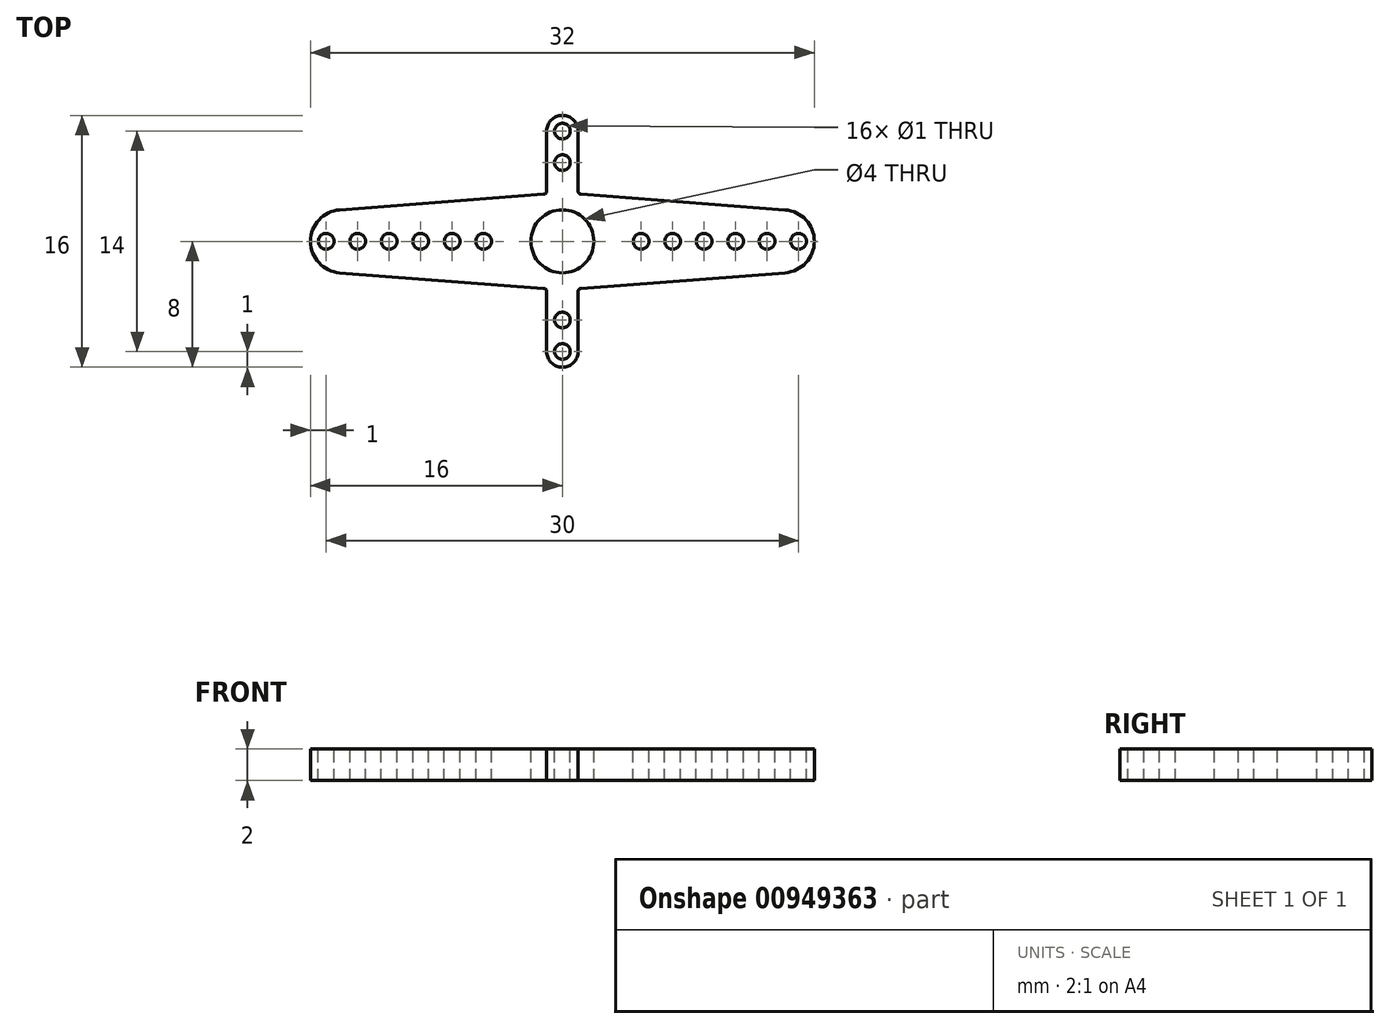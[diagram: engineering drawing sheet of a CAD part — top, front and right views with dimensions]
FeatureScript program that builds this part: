
annotation { "Feature Type Name" : "Feature", "Feature Type Description" : "" }
export const myFeature = defineFeature(function(context is Context, id is Id, definition is map)
    precondition{}
    {
        {
            var Q0;
            Q0=qCreatedBy(makeId("Top.planeOp"),FACE);
            var sketch = newSketch(context, id + "F0", { "sketchPlane" : qUnion([Q0])});
            skLineSegment(sketch, "E0", {"start": v(0, 0) * mm, "end": v(16, 0) * mm, "construction": true});
            skPoint(sketch, "E1", {"position": v(5, 0) * mm});
            skLineSegment(sketch, "E2", {"start": v(0, 0) * mm, "end": v(0, 8) * mm, "construction": true});
            skPoint(sketch, "E3", {"position": v(0, 5) * mm});
            skLineSegment(sketch, "E4", {"start": v(1, 7) * mm, "end": v(1, 3.19) * mm});
            skLineSegment(sketch, "E5", {"start": v(14.15, 2) * mm, "end": v(1.18, 2.99) * mm});
            skPoint(sketch, "E6.MirrorP", {"position": v(-5, 0) * mm});
            skLineSegment(sketch, "E7.MirrorCS", {"start": v(0, 0) * mm, "end": v(-16, 0) * mm, "construction": true});
            skLineSegment(sketch, "E8.MirrorCS", {"start": v(-14.15, 2) * mm, "end": v(-1.18, 2.99) * mm});
            skLineSegment(sketch, "E9.MirrorCS", {"start": v(-1, 7) * mm, "end": v(-1, 3.19) * mm});
            skPoint(sketch, "E10.visualSharp", {"position": v(1, 3) * mm});
            skArc(sketch, "E10.filletArc", {"start": v(1, 3.19) * mm, "mid": v(1.05, 3.05) * mm, "end": v(1.18, 2.99) * mm});
            skPoint(sketch, "E11.visualSharp", {"position": v(-1, 3) * mm});
            skArc(sketch, "E11.filletArc", {"start": v(-1.18, 2.99) * mm, "mid": v(-1.05, 3.05) * mm, "end": v(-1, 3.19) * mm});
            skArc(sketch, "E12", {"start": v(1, 7) * mm, "mid": v(0, 8) * mm, "end": v(-1, 7) * mm});
            skArc(sketch, "E13.MirrorCS", {"start": v(1, -3.19) * mm, "mid": v(1.05, -3.05) * mm, "end": v(1.18, -2.99) * mm});
            skArc(sketch, "E14.MirrorCS", {"start": v(-1.18, -2.99) * mm, "mid": v(-1.05, -3.05) * mm, "end": v(-1, -3.19) * mm});
            skPoint(sketch, "E15.MirrorP", {"position": v(0, -5) * mm});
            skLineSegment(sketch, "E16.MirrorCS", {"start": v(-1, -7) * mm, "end": v(-1, -3.19) * mm});
            skPoint(sketch, "E17.MirrorP", {"position": v(-1, -3) * mm});
            skLineSegment(sketch, "E18.MirrorCS", {"start": v(14.15, -2) * mm, "end": v(1.18, -2.99) * mm});
            skArc(sketch, "E19.MirrorCS", {"start": v(1, -7) * mm, "mid": v(0, -8) * mm, "end": v(-1, -7) * mm});
            skPoint(sketch, "E20.MirrorP", {"position": v(1, -3) * mm});
            skLineSegment(sketch, "E21.MirrorCS", {"start": v(1, -7) * mm, "end": v(1, -3.19) * mm});
            skLineSegment(sketch, "E22.MirrorCS", {"start": v(-14.15, -2) * mm, "end": v(-1.18, -2.99) * mm});
            skArc(sketch, "E23", {"start": v(14.15, -2) * mm, "mid": v(16, 0) * mm, "end": v(14.15, 2) * mm});
            skArc(sketch, "E24.MirrorCS", {"start": v(-14.15, -2) * mm, "mid": v(-16, 0) * mm, "end": v(-14.15, 2) * mm});
            skSolve(sketch);
        }
        {
            var Q0;
            Q0=makeQuery(id+"F0.imprint","IMPRINT",FACE,{"disambiguationData":[TD([[makeQuery(id+"F0.imprint","IMPRINT",EDGE,{"derivedFrom":sQuery(id+"F0.wireOp",EDGE,"E4")}),-1.0]])]});
            extrude(context, id + "F1", {"entities" : qUnion([Q0]), "depth" : 2 * mm, "offsetDistance" : 25 * mm});
        }
        {
            var Q0;
            Q0=makeQuery(id+"F1.opExtrude","CAP_FACE",FACE,{"disambiguationData":[OSD([sQuery(id+"F0.wireOp",EDGE,"E4"),sQuery(id+"F0.wireOp",EDGE,"E5"),sQuery(id+"F0.wireOp",EDGE,"E8.MirrorCS"),sQuery(id+"F0.wireOp",EDGE,"E9.MirrorCS"),sQuery(id+"F0.wireOp",EDGE,"E10.filletArc"),sQuery(id+"F0.wireOp",EDGE,"E11.filletArc"),sQuery(id+"F0.wireOp",EDGE,"E12"),sQuery(id+"F0.wireOp",EDGE,"E13.MirrorCS"),sQuery(id+"F0.wireOp",EDGE,"E14.MirrorCS"),sQuery(id+"F0.wireOp",EDGE,"E16.MirrorCS"),sQuery(id+"F0.wireOp",EDGE,"E18.MirrorCS"),sQuery(id+"F0.wireOp",EDGE,"E19.MirrorCS"),sQuery(id+"F0.wireOp",EDGE,"E21.MirrorCS"),sQuery(id+"F0.wireOp",EDGE,"E22.MirrorCS"),sQuery(id+"F0.wireOp",EDGE,"E23"),sQuery(id+"F0.wireOp",EDGE,"E24.MirrorCS")])],"isStart":false});
            var sketch = newSketch(context, id + "F2", { "sketchPlane" : qUnion([Q0])});
            skLineSegment(sketch, "E25", {"start": v(0, 0) * mm, "end": v(16, 0) * mm, "construction": true});
            skLineSegment(sketch, "E26", {"start": v(0, 0) * mm, "end": v(0, 8) * mm, "construction": true});
            skPoint(sketch, "E27", {"position": v(5, 0) * mm});
            skPoint(sketch, "E28", {"position": v(0, 5) * mm});
            skPoint(sketch, "E29.MirrorP", {"position": v(-5, 0) * mm});
            skPoint(sketch, "E30.MirrorP", {"position": v(0, -5) * mm});
            skPoint(sketch, "E31.1.0.0", {"position": v(7, 0) * mm});
            skPoint(sketch, "E31.2.0.0", {"position": v(9, 0) * mm});
            skPoint(sketch, "E31.3.0.0", {"position": v(11, 0) * mm});
            skPoint(sketch, "E31.4.0.0", {"position": v(13, 0) * mm});
            skPoint(sketch, "E31.5.0.0", {"position": v(15, 0) * mm});
            skLineSegment(sketch, "E31.direction1", {"start": v(5, 0) * mm, "end": v(7, 0) * mm, "construction": true});
            skPoint(sketch, "E32.1.0.0", {"position": v(-7, 0) * mm});
            skPoint(sketch, "E32.2.0.0", {"position": v(-9, 0) * mm});
            skPoint(sketch, "E32.3.0.0", {"position": v(-11, 0) * mm});
            skPoint(sketch, "E32.4.0.0", {"position": v(-13, 0) * mm});
            skPoint(sketch, "E32.5.0.0", {"position": v(-15, 0) * mm});
            skLineSegment(sketch, "E32.direction1", {"start": v(-5, 0) * mm, "end": v(-7, 0) * mm, "construction": true});
            skPoint(sketch, "E33", {"position": v(0, 7) * mm});
            skPoint(sketch, "E34.MirrorP", {"position": v(0, -7) * mm});
            skPoint(sketch, "E35", {"position": v(0, 0) * mm});
            skSolve(sketch);
        }
        {
            var Q0;
            Q0=sQuery(id+"F2.wireOp",VERTEX,"E27");
            var Q1;
            Q1=sQuery(id+"F2.wireOp",VERTEX,"E31.1.0.0");
            var Q2;
            Q2=sQuery(id+"F2.wireOp",VERTEX,"E31.2.0.0");
            var Q3;
            Q3=sQuery(id+"F2.wireOp",VERTEX,"E31.3.0.0");
            var Q4;
            Q4=sQuery(id+"F2.wireOp",VERTEX,"E31.4.0.0");
            var Q5;
            Q5=sQuery(id+"F2.wireOp",VERTEX,"E31.5.0.0");
            var Q6;
            Q6=sQuery(id+"F2.wireOp",VERTEX,"E28");
            var Q7;
            Q7=sQuery(id+"F2.wireOp",VERTEX,"E33");
            var Q8;
            Q8=sQuery(id+"F2.wireOp",VERTEX,"E29.MirrorP");
            var Q9;
            Q9=sQuery(id+"F2.wireOp",VERTEX,"E32.1.0.0");
            var Q10;
            Q10=sQuery(id+"F2.wireOp",VERTEX,"E32.2.0.0");
            var Q11;
            Q11=sQuery(id+"F2.wireOp",VERTEX,"E32.3.0.0");
            var Q12;
            Q12=sQuery(id+"F2.wireOp",VERTEX,"E32.4.0.0");
            var Q13;
            Q13=sQuery(id+"F2.wireOp",VERTEX,"E32.5.0.0");
            var Q14;
            Q14=sQuery(id+"F2.wireOp",VERTEX,"E30.MirrorP");
            var Q15;
            Q15=sQuery(id+"F2.wireOp",VERTEX,"E34.MirrorP");
            var Q16;
            Q16=makeQuery(id+"F1.opExtrude","SWEPT_BODY",BODY,{"disambiguationData":[OSD([sQuery(id+"F0.wireOp",EDGE,"E4"),sQuery(id+"F0.wireOp",EDGE,"E5"),sQuery(id+"F0.wireOp",EDGE,"E8.MirrorCS"),sQuery(id+"F0.wireOp",EDGE,"E9.MirrorCS"),sQuery(id+"F0.wireOp",EDGE,"E10.filletArc"),sQuery(id+"F0.wireOp",EDGE,"E11.filletArc"),sQuery(id+"F0.wireOp",EDGE,"E12"),sQuery(id+"F0.wireOp",EDGE,"E13.MirrorCS"),sQuery(id+"F0.wireOp",EDGE,"E14.MirrorCS"),sQuery(id+"F0.wireOp",EDGE,"E16.MirrorCS"),sQuery(id+"F0.wireOp",EDGE,"E18.MirrorCS"),sQuery(id+"F0.wireOp",EDGE,"E19.MirrorCS"),sQuery(id+"F0.wireOp",EDGE,"E21.MirrorCS"),sQuery(id+"F0.wireOp",EDGE,"E22.MirrorCS"),sQuery(id+"F0.wireOp",EDGE,"E23"),sQuery(id+"F0.wireOp",EDGE,"E24.MirrorCS")])]});
            hole(context, id + "F3", {"style" : HoleStyle.SIMPLE, "endStyle" : HoleEndStyle.THROUGH, "holeDiameter" : 1 * mm, "majorDiameter" : 5 * mm, "isTappedThrough" : true, "tappedDepth" : 12 * mm, "tapClearance" : 3, "locations" : qUnion([Q0, Q1, Q2, Q3, Q4, Q5, Q6, Q7, Q8, Q9, Q10, Q11, Q12, Q13, Q14, Q15]), "scope" : qUnion([Q16])});
        }
        {
            var Q0;
            Q0=makeQuery(id+"F1.opExtrude","CAP_FACE",FACE,{"disambiguationData":[OSD([sQuery(id+"F0.wireOp",EDGE,"E4"),sQuery(id+"F0.wireOp",EDGE,"E5"),sQuery(id+"F0.wireOp",EDGE,"E8.MirrorCS"),sQuery(id+"F0.wireOp",EDGE,"E9.MirrorCS"),sQuery(id+"F0.wireOp",EDGE,"E10.filletArc"),sQuery(id+"F0.wireOp",EDGE,"E11.filletArc"),sQuery(id+"F0.wireOp",EDGE,"E12"),sQuery(id+"F0.wireOp",EDGE,"E13.MirrorCS"),sQuery(id+"F0.wireOp",EDGE,"E14.MirrorCS"),sQuery(id+"F0.wireOp",EDGE,"E16.MirrorCS"),sQuery(id+"F0.wireOp",EDGE,"E18.MirrorCS"),sQuery(id+"F0.wireOp",EDGE,"E19.MirrorCS"),sQuery(id+"F0.wireOp",EDGE,"E21.MirrorCS"),sQuery(id+"F0.wireOp",EDGE,"E22.MirrorCS"),sQuery(id+"F0.wireOp",EDGE,"E23"),sQuery(id+"F0.wireOp",EDGE,"E24.MirrorCS")])],"isStart":false});
            var sketch = newSketch(context, id + "F4", { "sketchPlane" : qUnion([Q0])});
            skPoint(sketch, "E36", {"position": v(0, 0) * mm});
            skSolve(sketch);
        }
        {
            var Q0;
            Q0=sQuery(id+"F4.wireOp",VERTEX,"E36");
            var Q1;
            Q1=makeQuery(id+"F1.opExtrude","SWEPT_BODY",BODY,{"disambiguationData":[OSD([sQuery(id+"F0.wireOp",EDGE,"E4"),sQuery(id+"F0.wireOp",EDGE,"E5"),sQuery(id+"F0.wireOp",EDGE,"E8.MirrorCS"),sQuery(id+"F0.wireOp",EDGE,"E9.MirrorCS"),sQuery(id+"F0.wireOp",EDGE,"E10.filletArc"),sQuery(id+"F0.wireOp",EDGE,"E11.filletArc"),sQuery(id+"F0.wireOp",EDGE,"E12"),sQuery(id+"F0.wireOp",EDGE,"E13.MirrorCS"),sQuery(id+"F0.wireOp",EDGE,"E14.MirrorCS"),sQuery(id+"F0.wireOp",EDGE,"E16.MirrorCS"),sQuery(id+"F0.wireOp",EDGE,"E18.MirrorCS"),sQuery(id+"F0.wireOp",EDGE,"E19.MirrorCS"),sQuery(id+"F0.wireOp",EDGE,"E21.MirrorCS"),sQuery(id+"F0.wireOp",EDGE,"E22.MirrorCS"),sQuery(id+"F0.wireOp",EDGE,"E23"),sQuery(id+"F0.wireOp",EDGE,"E24.MirrorCS")])]});
            hole(context, id + "F5", {"style" : HoleStyle.SIMPLE, "endStyle" : HoleEndStyle.THROUGH, "holeDiameter" : 4 * mm, "majorDiameter" : 5 * mm, "isTappedThrough" : true, "tappedDepth" : 12 * mm, "tapClearance" : 3, "locations" : qUnion([Q0]), "scope" : qUnion([Q1])});
        }
    });
